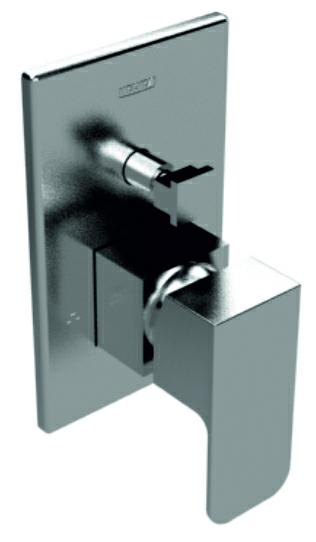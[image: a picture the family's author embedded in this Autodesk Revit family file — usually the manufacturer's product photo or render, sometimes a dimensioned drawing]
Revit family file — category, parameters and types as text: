
# Revit family: Monomando de Regadera E-793
name_source: partatom
category: Plumbing Fixtures
revit_build: Autodesk Revit 2015 (Build: 20140223_1515(x64)
units: mm (PartAtom-declared; Revit-internal decimal feet)

## types (1)
- E-793
    Brass Chromed = Brass
    Cartucho = Cartucho monomando cerámico con balanceo de presión Ø40mm
    Default Elevation = 1"
    Description = Monomando para Regadera y/o Tina con Balanceo de Presión con Desviador.
    Garantía = El producto HELVEX está garantizado como libre de defectos en materiales y procesos de fabricación. El producto HELVEX está garantizado, en lo que se refiere a los acabados; por un periodo de 10 años en los acabados cromo y duravex, y por 2 años en cabados diferentes al cromo, a partir de la fecha de compra indicada en la factura.
    Instalación = ½" - 14 NPT
    Manufacturer = HELVEX S.A. DE C.V.
    Model = E-793
    Operación = Para abrir el flujo de agua levante la palanca maneral y gire para regular la temperatura.
    Presión máxima de trabajo = 85.3 psi
    Presión mínima de trabajo = 14.2 psi
    Satin = Satín
    Support Base Diameter = 5"
    Total Height = 6"
    Type Comments = Monomando Squadra
    Type Image = E-793.jpg
    URL = http://www.helvex.com.mx

## geometry (parser evidence)
native form markers: Sweep x3
no freeform markers — native parametric forms only
